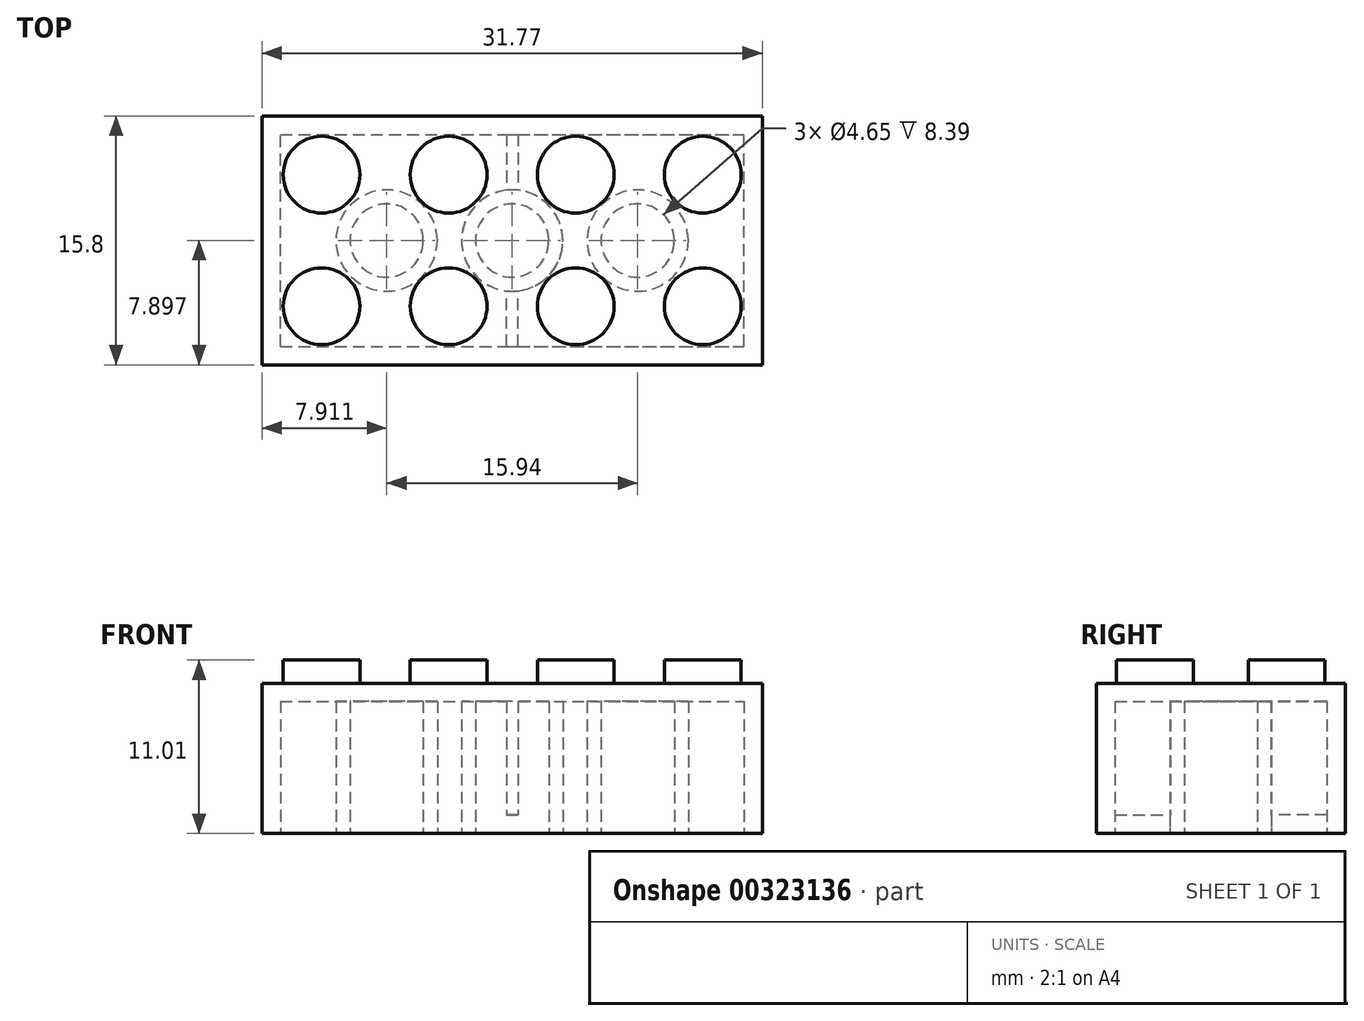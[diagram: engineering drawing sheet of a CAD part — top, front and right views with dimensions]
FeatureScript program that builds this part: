
annotation { "Feature Type Name" : "Feature", "Feature Type Description" : "" }
export const myFeature = defineFeature(function(context is Context, id is Id, definition is map)
    precondition{}
    {
        {
            var Q0;
            Q0=qCreatedBy(makeId("Top.planeOp"),FACE);
            var sketch = newSketch(context, id + "F0", { "sketchPlane" : qUnion([Q0])});
            skLineSegment(sketch, "E0.bottom", {"start": v(-13.15, 22.82) * mm, "end": v(18.62, 22.82) * mm});
            skLineSegment(sketch, "E0.top", {"start": v(-13.15, 7.02) * mm, "end": v(18.62, 7.02) * mm});
            skLineSegment(sketch, "E0.left", {"start": v(-13.15, 22.82) * mm, "end": v(-13.15, 7.02) * mm});
            skLineSegment(sketch, "E0.right", {"start": v(18.62, 22.82) * mm, "end": v(18.62, 7.02) * mm});
            skLineSegment(sketch, "E1.bottom", {"start": v(-11.98, 8.2) * mm, "end": v(17.45, 8.2) * mm});
            skLineSegment(sketch, "E1.top", {"start": v(-11.98, 21.65) * mm, "end": v(17.45, 21.65) * mm});
            skLineSegment(sketch, "E1.left", {"start": v(-11.98, 8.2) * mm, "end": v(-11.98, 21.65) * mm});
            skLineSegment(sketch, "E1.right", {"start": v(17.45, 8.2) * mm, "end": v(17.45, 21.65) * mm});
            skCircle(sketch, "E2", {"center": v(2.73, 14.92) * mm, "radius": 3.21 * mm});
            skCircle(sketch, "E3", {"center": v(10.7, 14.92) * mm, "radius": 3.21 * mm});
            skCircle(sketch, "E4", {"center": v(-5.24, 14.92) * mm, "radius": 3.21 * mm});
            skCircle(sketch, "E5", {"center": v(-5.24, 14.92) * mm, "radius": 2.32 * mm});
            skCircle(sketch, "E6", {"center": v(2.73, 14.92) * mm, "radius": 2.32 * mm});
            skCircle(sketch, "E7", {"center": v(10.7, 14.92) * mm, "radius": 2.32 * mm});
            skLineSegment(sketch, "E8", {"start": v(2.36, 8.2) * mm, "end": v(2.36, 11.72) * mm});
            skLineSegment(sketch, "E9", {"start": v(3.1, 8.2) * mm, "end": v(3.1, 11.72) * mm});
            skLineSegment(sketch, "E10", {"start": v(2.36, 21.65) * mm, "end": v(2.36, 18.11) * mm});
            skLineSegment(sketch, "E11", {"start": v(3.1, 21.65) * mm, "end": v(3.1, 18.11) * mm});
            skSolve(sketch);
        }
        {
            var Q0;
            Q0 = qSketchRegion(id + "F0", true);
            var Q1;
            {var subQ3=sQuery(id+"F0.wireOp",EDGE,"E1.left");Q1=makeQuery(id+"F0.imprint","IMPRINT",FACE,{"disambiguationData":[TD([[makeQuery(id+"F0.imprint","IMPRINT",EDGE,{"derivedFrom":subQ3}),-1.0]])]});}
            var Q2;
            {var subQ3=sQuery(id+"F0.wireOp",EDGE,"E1.right");Q2=makeQuery(id+"F0.imprint","IMPRINT",FACE,{"disambiguationData":[TD([[makeQuery(id+"F0.imprint","IMPRINT",EDGE,{"derivedFrom":subQ3}),1.0]])]});}
            var Q3;
            Q3=makeQuery(id+"F0.imprint","IMPRINT",FACE,{"disambiguationData":[TD([[makeQuery(id+"F0.imprint","IMPRINT",EDGE,{"derivedFrom":sQuery(id+"F0.wireOp",EDGE,"E7")}),1.0]])]});
            var Q4;
            Q4=makeQuery(id+"F0.imprint","IMPRINT",FACE,{"disambiguationData":[TD([[makeQuery(id+"F0.imprint","IMPRINT",EDGE,{"derivedFrom":sQuery(id+"F0.wireOp",EDGE,"E5")}),1.0]])]});
            var Q5;
            Q5=makeQuery(id+"F0.imprint","IMPRINT",FACE,{"disambiguationData":[TD([[makeQuery(id+"F0.imprint","IMPRINT",EDGE,{"derivedFrom":sQuery(id+"F0.wireOp",EDGE,"E6")}),1.0]])]});
            var Q6;
            Q6=makeQuery(id+"F0.imprint","IMPRINT",FACE,{"disambiguationData":[TD([[makeQuery(id+"F0.imprint","IMPRINT",EDGE,{"derivedFrom":sQuery(id+"F0.wireOp",EDGE,"E6")}),-1.0]])]});
            var Q7;
            {var subQ0=sQuery(id+"F0.wireOp",EDGE,"E10");Q7=makeQuery(id+"F0.imprint","IMPRINT",FACE,{"disambiguationData":[TD([[makeQuery(id+"F0.imprint","IMPRINT",EDGE,{"derivedFrom":subQ0}),1.0]])]});}
            var Q8;
            Q8=makeQuery(id+"F0.imprint","IMPRINT",FACE,{"disambiguationData":[TD([[makeQuery(id+"F0.imprint","IMPRINT",EDGE,{"derivedFrom":sQuery(id+"F0.wireOp",EDGE,"E3")}),1.0]])]});
            var Q9;
            Q9=makeQuery(id+"F0.imprint","IMPRINT",FACE,{"disambiguationData":[TD([[makeQuery(id+"F0.imprint","IMPRINT",EDGE,{"derivedFrom":sQuery(id+"F0.wireOp",EDGE,"E4")}),1.0]])]});
            var Q10;
            {var subQ0=sQuery(id+"F0.wireOp",EDGE,"E8");Q10=makeQuery(id+"F0.imprint","IMPRINT",FACE,{"disambiguationData":[TD([[makeQuery(id+"F0.imprint","IMPRINT",EDGE,{"derivedFrom":subQ0}),-1.0]])]});}
            extrude(context, id + "F1", {"entities" : qUnion([Q0, Q1, Q2, Q3, Q4, Q5, Q6, Q7, Q8, Q9, Q10]), "depth" : 9.53 * mm});
        }
        {
            var Q0;
            {var subQ3=sQuery(id+"F0.wireOp",EDGE,"E1.left");Q0=makeQuery(id+"F0.imprint","IMPRINT",FACE,{"disambiguationData":[TD([[makeQuery(id+"F0.imprint","IMPRINT",EDGE,{"derivedFrom":subQ3}),-1.0]])]});}
            var Q1;
            {var subQ3=sQuery(id+"F0.wireOp",EDGE,"E1.right");Q1=makeQuery(id+"F0.imprint","IMPRINT",FACE,{"disambiguationData":[TD([[makeQuery(id+"F0.imprint","IMPRINT",EDGE,{"derivedFrom":subQ3}),1.0]])]});}
            var Q2;
            Q2=makeQuery(id+"F0.imprint","IMPRINT",FACE,{"disambiguationData":[TD([[makeQuery(id+"F0.imprint","IMPRINT",EDGE,{"derivedFrom":sQuery(id+"F0.wireOp",EDGE,"E7")}),1.0]])]});
            var Q3;
            Q3=makeQuery(id+"F0.imprint","IMPRINT",FACE,{"disambiguationData":[TD([[makeQuery(id+"F0.imprint","IMPRINT",EDGE,{"derivedFrom":sQuery(id+"F0.wireOp",EDGE,"E6")}),1.0]])]});
            var Q4;
            Q4=makeQuery(id+"F0.imprint","IMPRINT",FACE,{"disambiguationData":[TD([[makeQuery(id+"F0.imprint","IMPRINT",EDGE,{"derivedFrom":sQuery(id+"F0.wireOp",EDGE,"E5")}),1.0]])]});
            extrude(context, id + "F2", {"entities" : qUnion([Q0, Q1, Q2, Q3, Q4]), "operationType" : NewBodyOperationType.REMOVE, "depth" : 8.4 * mm});
        }
        {
            var Q0;
            {var subQ0=sQuery(id+"F0.wireOp",EDGE,"E8");Q0=makeQuery(id+"F0.imprint","IMPRINT",FACE,{"disambiguationData":[TD([[makeQuery(id+"F0.imprint","IMPRINT",EDGE,{"derivedFrom":subQ0}),-1.0]])]});}
            var Q1;
            {var subQ0=sQuery(id+"F0.wireOp",EDGE,"E10");Q1=makeQuery(id+"F0.imprint","IMPRINT",FACE,{"disambiguationData":[TD([[makeQuery(id+"F0.imprint","IMPRINT",EDGE,{"derivedFrom":subQ0}),1.0]])]});}
            extrude(context, id + "F3", {"entities" : qUnion([Q0, Q1]), "operationType" : NewBodyOperationType.REMOVE, "depth" : 1.17 * mm});
        }
        {
            var Q0;
            Q0=makeQuery(id+"F1.opExtrude","CAP_FACE",FACE,{"disambiguationData":[OSD([sQuery(id+"F0.wireOp",EDGE,"E0.bottom"),sQuery(id+"F0.wireOp",EDGE,"E0.top"),sQuery(id+"F0.wireOp",EDGE,"E0.left"),sQuery(id+"F0.wireOp",EDGE,"E0.right")])],"isStart":false});
            var sketch = newSketch(context, id + "F4", { "sketchPlane" : qUnion([Q0])});
            skCircle(sketch, "E12", {"center": v(-9.37, 19.1) * mm, "radius": 2.44 * mm});
            skCircle(sketch, "E13", {"center": v(-1.3, 19.1) * mm, "radius": 2.44 * mm});
            skCircle(sketch, "E14", {"center": v(6.77, 19.1) * mm, "radius": 2.44 * mm});
            skCircle(sketch, "E15", {"center": v(14.84, 19.1) * mm, "radius": 2.44 * mm});
            skCircle(sketch, "E16", {"center": v(-9.37, 10.74) * mm, "radius": 2.44 * mm});
            skCircle(sketch, "E17", {"center": v(-1.3, 10.74) * mm, "radius": 2.44 * mm});
            skCircle(sketch, "E18", {"center": v(6.77, 10.74) * mm, "radius": 2.44 * mm});
            skCircle(sketch, "E19", {"center": v(14.84, 10.74) * mm, "radius": 2.44 * mm});
            skSolve(sketch);
        }
        {
            var Q0;
            Q0=makeQuery(id+"F4.imprint","IMPRINT",FACE,{"disambiguationData":[TD([[makeQuery(id+"F4.imprint","IMPRINT",EDGE,{"derivedFrom":sQuery(id+"F4.wireOp",EDGE,"E12")}),1.0]])]});
            var Q1;
            Q1=makeQuery(id+"F4.imprint","IMPRINT",FACE,{"disambiguationData":[TD([[makeQuery(id+"F4.imprint","IMPRINT",EDGE,{"derivedFrom":sQuery(id+"F4.wireOp",EDGE,"E16")}),1.0]])]});
            var Q2;
            Q2=makeQuery(id+"F4.imprint","IMPRINT",FACE,{"disambiguationData":[TD([[makeQuery(id+"F4.imprint","IMPRINT",EDGE,{"derivedFrom":sQuery(id+"F4.wireOp",EDGE,"E13")}),1.0]])]});
            var Q3;
            Q3=makeQuery(id+"F4.imprint","IMPRINT",FACE,{"disambiguationData":[TD([[makeQuery(id+"F4.imprint","IMPRINT",EDGE,{"derivedFrom":sQuery(id+"F4.wireOp",EDGE,"E17")}),1.0]])]});
            var Q4;
            Q4=makeQuery(id+"F4.imprint","IMPRINT",FACE,{"disambiguationData":[TD([[makeQuery(id+"F4.imprint","IMPRINT",EDGE,{"derivedFrom":sQuery(id+"F4.wireOp",EDGE,"E14")}),1.0]])]});
            var Q5;
            Q5=makeQuery(id+"F4.imprint","IMPRINT",FACE,{"disambiguationData":[TD([[makeQuery(id+"F4.imprint","IMPRINT",EDGE,{"derivedFrom":sQuery(id+"F4.wireOp",EDGE,"E18")}),1.0]])]});
            var Q6;
            Q6=makeQuery(id+"F4.imprint","IMPRINT",FACE,{"disambiguationData":[TD([[makeQuery(id+"F4.imprint","IMPRINT",EDGE,{"derivedFrom":sQuery(id+"F4.wireOp",EDGE,"E15")}),1.0]])]});
            var Q7;
            Q7=makeQuery(id+"F4.imprint","IMPRINT",FACE,{"disambiguationData":[TD([[makeQuery(id+"F4.imprint","IMPRINT",EDGE,{"derivedFrom":sQuery(id+"F4.wireOp",EDGE,"E19")}),1.0]])]});
            extrude(context, id + "F5", {"entities" : qUnion([Q0, Q1, Q2, Q3, Q4, Q5, Q6, Q7]), "operationType" : NewBodyOperationType.ADD, "depth" : 1.48 * mm});
        }
    });
